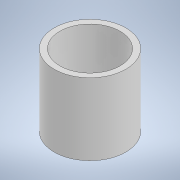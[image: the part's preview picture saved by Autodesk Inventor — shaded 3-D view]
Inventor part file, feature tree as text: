
AUTODESK INVENTOR PART (.ipt)
format: ipt  version: 2020 (Build 240168000, 168)  size: 101,888 bytes
history: native  units: in
note: dims shown in document units (in); Inventor stores cm internally (conversion verified against a paired STEP export)
features: extrude x2, sketch x2
ambient origin geometry x8: Origin, YZ Plane, XZ Plane, XY Plane, X Axis, Y Axis, Z Axis, Center Point
bodies: Solid1 (feature_tree)
feature tree (4):
  extrude  "Extrusion1"  Depth=0.3937in TaperAngle=0.0deg
  extrude  "Extrusion2"  Depth=3.5521in
  sketch  "Sketch1"  dims[d0=3.937in d1=0.3937in d2=0.0in]
  sketch  "Sketch2"  dims[d3=3.3071in d4=3.937in d5=3.5521in d6=0.0in]
